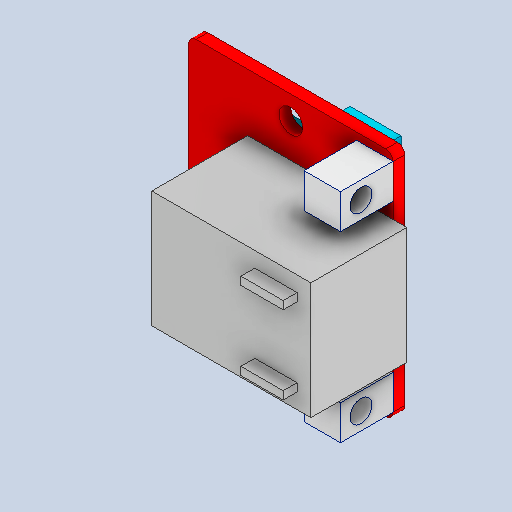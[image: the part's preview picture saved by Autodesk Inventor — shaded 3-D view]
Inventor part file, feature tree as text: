
AUTODESK INVENTOR PART (.ipt)
format: ipt  version: 2024.2 (Build 282272000, 272)  size: 367,616 bytes
history: native  units: mm
features: extrude x7, sketch x7, projected_geometry x2, fillet x1
ambient origin geometry x8: Origin, YZ Plane, XZ Plane, XY Plane, X Axis, Y Axis, Z Axis, Center Point
bodies: Solid1 (feature_tree), Solid2 (feature_tree), Solid3 (feature_tree), Solid4 (feature_tree), Solid5 (feature_tree)
feature tree (17):
  extrude  "Extrusion1"  Depth=31.75mm
  extrude  "Extrusion2"  Depth=3.26mm
  extrude  "Extrusion3"  Depth=16.0mm
  extrude  "Extrusion4"  Depth=1.89mm
  extrude  "Extrusion5"  Depth=5.8mm
  extrude  "Extrusion6"  Depth=1.1mm
  extrude  "Extrusion7"  Depth=4.75mm
  fillet  "Fillet1"  Radius=25.05mm
  sketch  "Sketch1"  dims[d0=28.0mm d1=31.75mm]
  sketch  "Sketch2"  dims[d2=25.4mm d3=3.26mm]
  sketch  "Sketch3"  dims[d4=1.6mm d5=0.0mm d6=16.0mm]
  projected_geometry  "Projected Loop1"
  sketch  "Sketch4"  dims[d7=21.8mm d8=1.89mm]
  projected_geometry  "Projected Loop2"
  sketch  "Sketch5"  dims[d9=13.15mm d10=0.0mm d11=5.8mm]
  sketch  "Sketch6"  dims[d12=3.2mm d13=1.1mm]
  sketch  "Sketch7"  dims[d14=1.9mm d15=0.0mm d16=4.75mm d18=25.05mm d19=7.2mm d20=0.0mm d21=3.0mm d22=4.4mm d23=7.2mm d24=0.0mm d25=15.3mm d26=3.0mm d27=3.3mm d28=2.0mm d29=0.0mm d30=1.0mm d31=2.5mm d32=2.5mm d33=5.0mm d34=7.0mm d35=18.0mm d36=2.0mm d37=0.0mm d38=1.0mm]
